# Revit family: Hook-BathrobeHolderDouble-Vitra-JunoClassicSeries-A44423
name_source: partatom
category: Plumbing Fixtures
revit_build: Autodesk Revit 2017 (Build: 20160225_1515(x64)
units: mm (PartAtom-declared; Revit-internal decimal feet)

## family parameters
Cut with Voids When Loaded = No
Host = Face
OmniClass Number = 23.45.00.00
OmniClass Title = Sanitary, Laundry, and Cleaning Equipment
Part Type = Normal
Room Calculation Point = No
Round Connector Dimension = Use Diameter
Shared = Yes

## types (6) — shared parameters
BIMobject category = Furniture - Hooks & Hangers
Brand = VitrA
CW Connection = No
Description = Juno Classic Hook Bathrobe Holder Double
Design country = Turkey
HW Connection = No
IFC Classification = Sanitary Terminal
Manufacturer = Vitra
Manufacturer name = Vitra
Masterformat 2014 Code = 41 23 19
Masterformat 2014 Description = Hooks
Mounting type = Wall Mounted
NBS Referans Code = 35-75-18
NBS Referans Description = Clothes Hooks
Nominal Depth (mm) = 63 mm
Nominal Height (mm) = 70 mm  [stored 0.229659 ft]
Nominal Width (mm) = 70 mm  [stored 0.229659 ft]
OmniClass Code = 23-31 25 27
OmniClass Description = Robe Hooks
Product Type = Hook Bathrobe Holder
Product certification = https://www.vitraglobal.com
Product family = Juno Classic Series
Product group = Hook Bathrobe Holder
UNSPSC Description = Furniture and Furnishings
URL = https://vitraglobal.com
Uniclass 1.4 Code = L41821
Uniclass 1.4 Description = Fasteners, stays, hooks
Uniclass 2.0 Code = PR-35-75-18
Uniclass 2.0 Description = Clothes Hooks
Uniclass 2015 Code = Pr_40_30_78_15
Uniclass 2015 Name = Clothes hooks
Uniformat II Code = E20
Uniformat II Description = FURNISHINGS
Vent Connection = No
Warranty Period (Year) = 5 years
Waste Connection = No
Weight Net (kg) = 0.8
Youtube = https://www.youtube.com
zero-valued in all types: Default Elevation

## per-type parameters (varying)
| type | Article No. (default) | Coating Material | Color | Model | Product SKU | Product url | Technical description |
| Hook-BathrobeHolderDouble-Vitra-JunoClassicSeries-A44423 | A44423 | Chrome | Chrome | A44423 | A44423 | https://www.vitra.com.tr | https://www.vitra.com.tr |
| Hook-BathrobeHolderDouble-Vitra-JunoClassicSeries-A4442323 | A4442323 | Gold | Gold | A4442323 | A4442323 | https://www.vitra.com.tr | https://www.vitra.com.tr |
| Hook-BathrobeHolderDouble-Vitra-JunoClassicSeries-A4442326 | A4442326 | Gold | Copper | A4442326 | A4442326 | https://www.vitra.com.tr | https://www.vitra.com.tr |
| Hook-BathrobeHolderDouble-Vitra-JunoClassicSeries-A44423EXP | A44423EXP | Chrome | Chrome | A44423EXP | A44423EXP | https://www.vitraglobal.com | https://www.vitraglobal.com |
| Hook-BathrobeHolderDouble-Vitra-JunoClassicSeries-A4442323EXP | A4442323EXP | Gold | Gold | A4442323EXP | A4442323EXP | https://www.vitraglobal.com | https://www.vitraglobal.com |
| Hook-BathrobeHolderDouble-Vitra-JunoClassicSeries-A4442326EXP | A4442326EXP | Gold | Copper | A4442326EXP | A4442326EXP | https://www.vitraglobal.com | https://www.vitraglobal.com |

note: [stored X ft] marks values corroborated as IEEE doubles in the binary element streams (Revit-internal decimal feet)

## geometry (parser evidence)
native form markers: Sweep x2
no freeform markers — native parametric forms only
